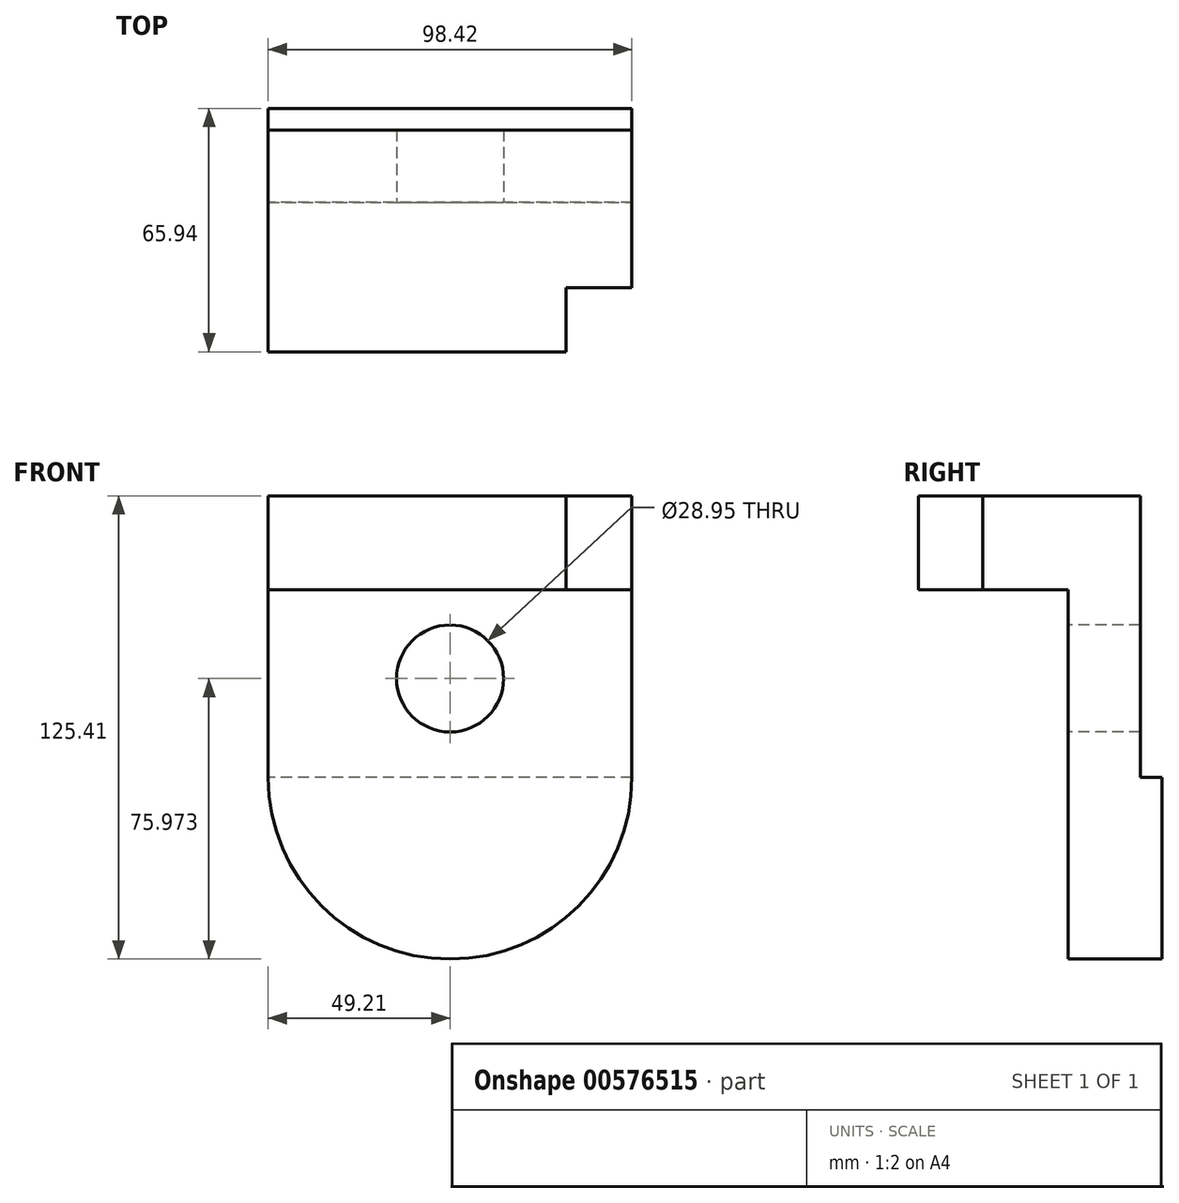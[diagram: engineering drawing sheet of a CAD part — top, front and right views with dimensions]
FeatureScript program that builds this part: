
annotation { "Feature Type Name" : "Feature", "Feature Type Description" : "" }
export const myFeature = defineFeature(function(context is Context, id is Id, definition is map)
    precondition{}
    {
        {
            var Q0;
            Q0=qCreatedBy(makeId("Top.planeOp"),FACE);
            var sketch = newSketch(context, id + "F0", { "sketchPlane" : qUnion([Q0])});
            skLineSegment(sketch, "E0.bottom", {"start": v(-49.21, -30.03) * mm, "end": v(49.21, -30.03) * mm});
            skLineSegment(sketch, "E0.top", {"start": v(-49.21, 30.03) * mm, "end": v(49.21, 30.03) * mm});
            skLineSegment(sketch, "E0.left", {"start": v(-49.21, -30.03) * mm, "end": v(-49.21, 30.03) * mm});
            skLineSegment(sketch, "E0.right", {"start": v(49.21, -30.03) * mm, "end": v(49.21, 30.03) * mm});
            skPoint(sketch, "E0.middle", {"position": v(0, 0) * mm});
            skSolve(sketch);
        }
        {
            var Q0;
            Q0=makeQuery(id+"F0.imprint","IMPRINT",FACE,{"disambiguationData":[TD([[makeQuery(id+"F0.imprint","IMPRINT",EDGE,{"derivedFrom":sQuery(id+"F0.wireOp",EDGE,"E0.bottom")}),1.0]])]});
            extrude(context, id + "F1", {"entities" : qUnion([Q0]), "depth" : 25.4 * mm, "offsetDistance" : 25.4 * mm});
        }
        {
            var Q0;
            Q0=qCreatedBy(makeId("Top.planeOp"),FACE);
            var sketch = newSketch(context, id + "F2", { "sketchPlane" : qUnion([Q0])});
            skLineSegment(sketch, "E1.bottom", {"start": v(49.21, -30.45) * mm, "end": v(31.43, -30.45) * mm});
            skLineSegment(sketch, "E1.top", {"start": v(49.21, -12.67) * mm, "end": v(31.43, -12.67) * mm});
            skLineSegment(sketch, "E1.left", {"start": v(49.21, -30.45) * mm, "end": v(49.21, -12.67) * mm});
            skLineSegment(sketch, "E1.right", {"start": v(31.43, -30.45) * mm, "end": v(31.43, -12.67) * mm});
            skSolve(sketch);
        }
        {
            var Q0;
            Q0=makeQuery(id+"F2.imprint","IMPRINT",FACE,{"disambiguationData":[TD([[makeQuery(id+"F2.imprint","IMPRINT",EDGE,{"derivedFrom":sQuery(id+"F2.wireOp",EDGE,"E1.bottom")}),-1.0]])]});
            extrude(context, id + "F3", {"entities" : qUnion([Q0]), "operationType" : NewBodyOperationType.REMOVE, "depth" : 25.4 * mm, "offsetDistance" : 25.4 * mm});
        }
        {
            var Q0;
            Q0=qCreatedBy(makeId("Top.planeOp"),FACE);
            var sketch = newSketch(context, id + "F4", { "sketchPlane" : qUnion([Q0])});
            skLineSegment(sketch, "E2.bottom", {"start": v(49.21, 30.03) * mm, "end": v(-49.21, 30.03) * mm});
            skLineSegment(sketch, "E2.top", {"start": v(49.21, 10.51) * mm, "end": v(-49.21, 10.51) * mm});
            skLineSegment(sketch, "E2.left", {"start": v(49.21, 30.03) * mm, "end": v(49.21, 10.51) * mm});
            skLineSegment(sketch, "E2.right", {"start": v(-49.21, 30.03) * mm, "end": v(-49.21, 10.51) * mm});
            skSolve(sketch);
        }
        {
            var Q0;
            Q0=makeQuery(id+"F4.imprint","IMPRINT",FACE,{"disambiguationData":[TD([[makeQuery(id+"F4.imprint","IMPRINT",EDGE,{"derivedFrom":sQuery(id+"F4.wireOp",EDGE,"E2.bottom")}),1.0]])]});
            extrude(context, id + "F5", {"entities" : qUnion([Q0]), "operationType" : NewBodyOperationType.ADD, "oppositeDirection" : true, "depth" : 50.8 * mm, "offsetDistance" : 25.4 * mm});
        }
        {
            var Q0;
            Q0=qCreatedBy(makeId("Front.planeOp"),FACE);
            var sketch = newSketch(context, id + "F6", { "sketchPlane" : qUnion([Q0])});
            skCircle(sketch, "E3", {"center": v(0, -24.04) * mm, "radius": 14.48 * mm});
            skSolve(sketch);
        }
        {
            var Q0;
            Q0=makeQuery(id+"F6.imprint","IMPRINT",FACE,{"disambiguationData":[TD([[makeQuery(id+"F6.imprint","IMPRINT",EDGE,{"derivedFrom":sQuery(id+"F6.wireOp",EDGE,"E3")}),1.0]])]});
            extrude(context, id + "F7", {"entities" : qUnion([Q0]), "operationType" : NewBodyOperationType.REMOVE, "oppositeDirection" : true, "depth" : 50.8 * mm, "offsetDistance" : 25.4 * mm});
        }
        {
            var Q0;
            Q0=makeQuery(id+"F5.opExtrude","SWEPT_FACE",FACE,{"disambiguationData":[OSD([sQuery(id+"F4.wireOp",EDGE,"E2.top")])]});
            var sketch = newSketch(context, id + "F8", { "sketchPlane" : qUnion([Q0])});
            skCircle(sketch, "E4", {"center": v(0, -50.8) * mm, "radius": 49.21 * mm});
            skLineSegment(sketch, "E5", {"start": v(49.21, -50.8) * mm, "end": v(-49.21, -50.8) * mm});
            skSolve(sketch);
        }
        {
            var Q0;
            {var subQ0=sQuery(id+"F8.wireOp",EDGE,"E5");Q0=makeQuery(id+"F8.imprint","IMPRINT",FACE,{"disambiguationData":[TD([[makeQuery(id+"F8.imprint","IMPRINT",EDGE,{"derivedFrom":subQ0}),1.0]])]});}
            extrude(context, id + "F9", {"entities" : qUnion([Q0]), "operationType" : NewBodyOperationType.ADD, "oppositeDirection" : true, "depth" : 25.4 * mm, "offsetDistance" : 25.4 * mm});
        }
    });
